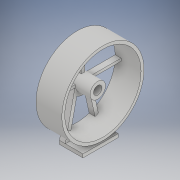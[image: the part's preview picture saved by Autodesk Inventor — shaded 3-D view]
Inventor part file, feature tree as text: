
AUTODESK INVENTOR PART (.ipt)
format: ipt  version: 2019 (Build 230136000, 136)  size: 253,440 bytes
history: native  units: in
note: dims shown in document units (in); Inventor stores cm internally (conversion verified against a paired STEP export)
features: sketch x14, extrude x12, projected_geometry x6
ambient origin geometry x8: Origin, YZ Plane, XZ Plane, XY Plane, X Axis, Y Axis, Z Axis, Center Point
bodies: Solid1 (feature_tree)
feature tree (32):
  extrude  "Extrusion1"  Depth=0.15in
  extrude  "Extrusion2"  Depth=0.1in TaperAngle=0.0deg
  extrude  "Extrusion3"  Depth=0.75in
  sketch  "Sketch6"  dims[d8=0.15in d9=0.25in d10=0.0in]
  extrude  "Extrusion7"  Depth=0.25in TaperAngle=0.0deg
  extrude  "Extrusion9"  Depth=0.875in TaperAngle=0.0deg
  extrude  "Extrusion10"  Depth=0.115in
  extrude  "Extrusion11"  Depth=0.05in
  extrude  "Extrusion12"  Depth=0.115in
  extrude  "Extrusion14"  Depth=0.05in
  extrude  "Extrusion15"  TaperAngle=0.0deg  [1 undecoded]
  extrude  "Extrusion16"  TaperAngle=0.0deg  [1 undecoded]
  sketch  "Sketch22"  dims[d48=3.5in]
  extrude  "Extrusion17"  Depth=0.1in
  sketch  "Sketch1"  dims[d0=0.36in d1=0.15in]
  sketch  "Sketch2"  dims[d2=0.78in d3=0.0in d4=0.1in d5=0.0in]
  sketch  "Sketch3"  dims[d6=1.5in d7=0.75in]
  sketch  "Sketch10"  dims[d20=0.5315in d28=0.875in d29=0.0in]
  sketch  "Sketch13"  dims[d32=0.115in d33=0.115in]
  sketch  "Sketch14"  dims[d34=0.0675in d35=0.05in]
  projected_geometry  "Projected Loop9"
  projected_geometry  "Projected Loop10"
  projected_geometry  "Projected Loop11"
  projected_geometry  "Projected Loop12"
  sketch  "Sketch15"  dims[d36=0.115in d37=0.115in]
  sketch  "Sketch16"  dims[d38=0.068in d39=0.05in]
  sketch  "Sketch19"  dims[d40=0.15in d41=0.0in d42=0.0in]
  sketch  "Sketch20"  dims[d43=0.0in d44=0.0in]
  projected_geometry  "Projected Loop13"
  sketch  "Sketch21"  dims[d45=0.1in d46=0.0in d47=3.25in]
  projected_geometry  "Projected Loop14"
  sketch  "Sketch23"  dims[d49=0.1in d50=0.0in d51=3.25in d52=1.0in d53=0.0in d82=0.25in d83=0.0in d84=0.25in d85=0.0in d86=0.25in d87=0.0in d88=0.75in d89=0.0in]
note: 2 required parameter values undecoded (feature->parameter linkage not recoverable at this tier; creation-order binding heuristic only, values carry confidence <= 0.55)
